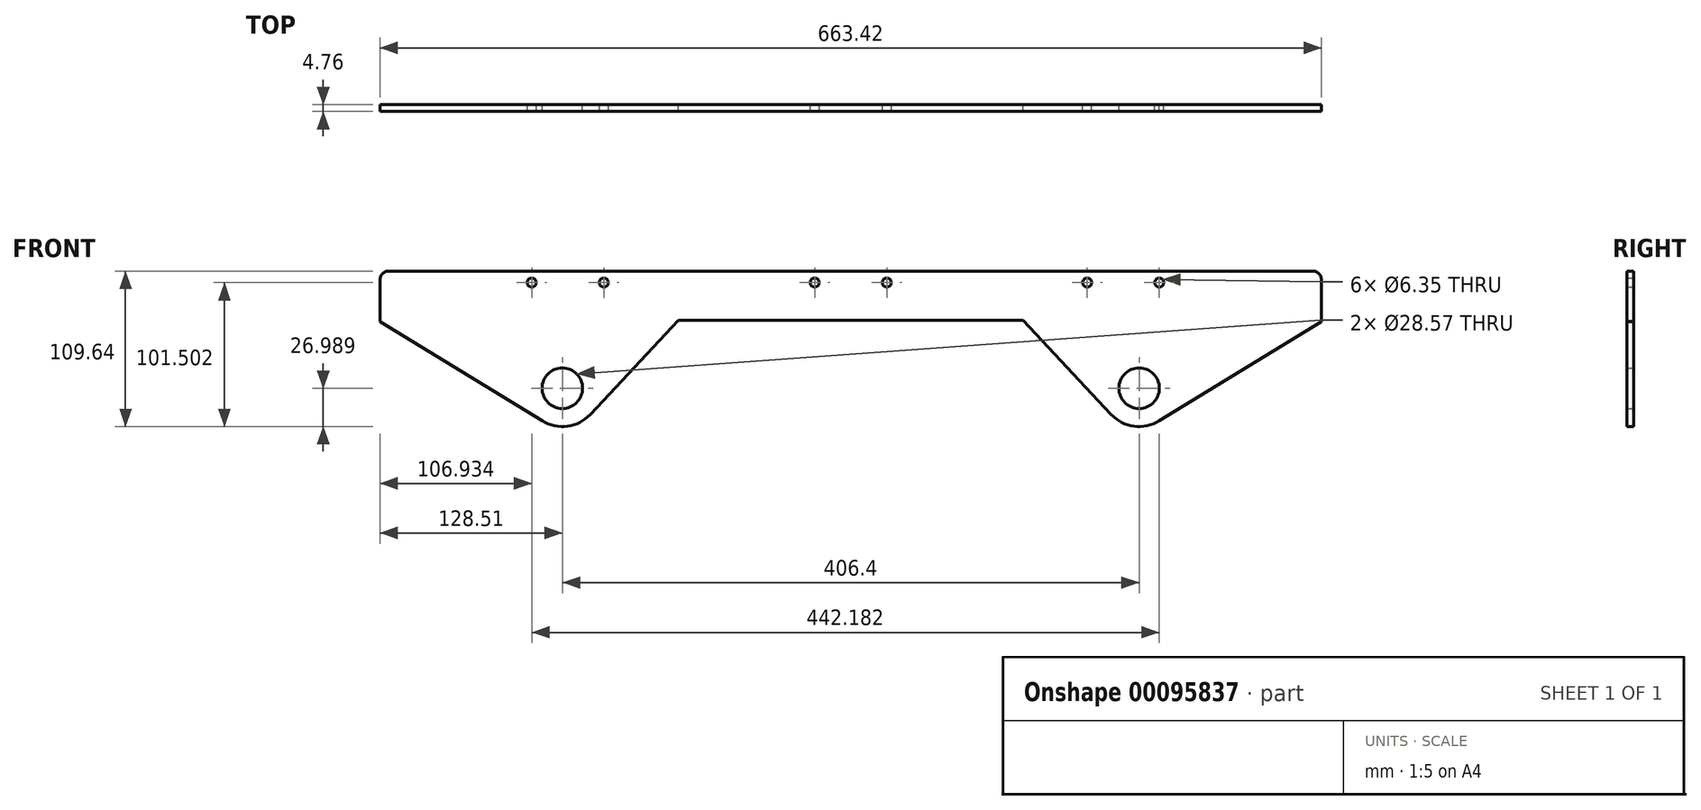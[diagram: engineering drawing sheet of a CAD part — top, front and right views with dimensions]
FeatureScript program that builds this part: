
annotation { "Feature Type Name" : "Feature", "Feature Type Description" : "" }
export const myFeature = defineFeature(function(context is Context, id is Id, definition is map)
    precondition{}
    {
        {
            var Q0;
            Q0=qCreatedBy(makeId("Front.planeOp"),FACE);
            var sketch = newSketch(context, id + "F0", { "sketchPlane" : qUnion([Q0])});
            skLineSegment(sketch, "E0", {"start": v(678.42, -37.96) * mm, "end": v(-454, -37.96) * mm, "construction": true});
            skLineSegment(sketch, "E1", {"start": v(0, -37.96) * mm, "end": v(0, 332.54) * mm, "construction": true});
            skCircle(sketch, "E2", {"center": v(217.4, 112.75) * mm, "radius": 3.18 * mm});
            skCircle(sketch, "E3", {"center": v(166.6, 112.75) * mm, "radius": 3.18 * mm});
            skCircle(sketch, "E4", {"center": v(25.4, 112.75) * mm, "radius": 3.18 * mm});
            skLineSegment(sketch, "E5", {"start": v(331.7, 85.33) * mm, "end": v(331.7, 114.54) * mm});
            skPoint(sketch, "E6.visualSharp", {"position": v(331.7, 119.1) * mm});
            skArc(sketch, "E6.filletArc", {"start": v(331.7, 114.54) * mm, "mid": v(329.85, 119.03) * mm, "end": v(325.36, 120.9) * mm});
            skPoint(sketch, "E7.orphan", {"position": v(0, -22.86) * mm});
            skLineSegment(sketch, "E8", {"start": v(325.36, 120.9) * mm, "end": v(0, 120.9) * mm});
            skLineSegment(sketch, "E9.MirrorCS", {"start": v(-325.36, 120.9) * mm, "end": v(0, 120.9) * mm});
            skArc(sketch, "E10.MirrorCS", {"start": v(-331.7, 114.54) * mm, "mid": v(-329.85, 119.03) * mm, "end": v(-325.36, 120.9) * mm});
            skLineSegment(sketch, "E11.MirrorCS", {"start": v(-331.7, 85.33) * mm, "end": v(-331.7, 114.54) * mm});
            skCircle(sketch, "E12.MirrorC", {"center": v(-25.4, 112.75) * mm, "radius": 3.18 * mm});
            skCircle(sketch, "E13.MirrorC", {"center": v(-173.98, 112.75) * mm, "radius": 3.18 * mm});
            skCircle(sketch, "E14.MirrorC", {"center": v(-224.78, 112.75) * mm, "radius": 3.18 * mm});
            skLineSegment(sketch, "E15", {"start": v(338.06, -37.96) * mm, "end": v(720.92, -140.55) * mm, "construction": true});
            skLineSegment(sketch, "E16", {"start": v(338.06, -37.96) * mm, "end": v(354.5, 23.38) * mm, "construction": true});
            skLineSegment(sketch, "E17", {"start": v(354.5, 23.38) * mm, "end": v(391.3, 13.51) * mm, "construction": true});
            skLineSegment(sketch, "E18", {"start": v(391.3, 13.51) * mm, "end": v(374.86, -47.82) * mm, "construction": true});
            skLineSegment(sketch, "E19", {"start": v(338.06, -37.96) * mm, "end": v(368.5, 75.63) * mm, "construction": true});
            skLineSegment(sketch, "E20", {"start": v(368.5, 75.63) * mm, "end": v(497.3, 41.12) * mm, "construction": true});
            skLineSegment(sketch, "E21", {"start": v(497.3, 41.12) * mm, "end": v(466.86, -72.47) * mm, "construction": true});
            skLineSegment(sketch, "E22", {"start": v(338.06, -37.96) * mm, "end": v(1103.17, -37.96) * mm});
            skCircle(sketch, "E23", {"center": v(203.2, 38.24) * mm, "radius": 14.29 * mm});
            skCircle(sketch, "E24", {"center": v(203.2, 38.24) * mm, "radius": 76.2 * mm, "construction": true});
            skArc(sketch, "E25.0", {"start": v(183.5, 19.79) * mm, "mid": v(199.6, 11.5) * mm, "end": v(217.3, 15.23) * mm});
            skLineSegment(sketch, "E26", {"start": v(331.7, 85.33) * mm, "end": v(217.3, 15.23) * mm});
            skLineSegment(sketch, "E27", {"start": v(0, 120.9) * mm, "end": v(0, 86.1) * mm, "construction": true});
            skLineSegment(sketch, "E28", {"start": v(0, 86.1) * mm, "end": v(121.38, 86.1) * mm});
            skLineSegment(sketch, "E29", {"start": v(121.38, 86.1) * mm, "end": v(183.5, 19.79) * mm});
            skLineSegment(sketch, "E30.MirrorCS", {"start": v(0, 86.1) * mm, "end": v(-121.38, 86.1) * mm});
            skLineSegment(sketch, "E31.MirrorCS", {"start": v(-121.38, 86.1) * mm, "end": v(-183.5, 19.79) * mm});
            skArc(sketch, "E32.MirrorCS", {"start": v(-183.5, 19.79) * mm, "mid": v(-199.6, 11.5) * mm, "end": v(-217.3, 15.23) * mm});
            skCircle(sketch, "E33.MirrorC", {"center": v(-203.2, 38.24) * mm, "radius": 14.29 * mm});
            skLineSegment(sketch, "E34.MirrorCS", {"start": v(-331.7, 85.33) * mm, "end": v(-217.3, 15.23) * mm});
            skCircle(sketch, "E35.MirrorC", {"center": v(-203.2, 38.24) * mm, "radius": 76.2 * mm, "construction": true});
            skSolve(sketch);
        }
        {
            var Q0;
            Q0=makeQuery(id+"F0.imprint","IMPRINT",FACE,{"disambiguationData":[TD([[makeQuery(id+"F0.imprint","IMPRINT",EDGE,{"derivedFrom":sQuery(id+"F0.wireOp",EDGE,"2147f539-64ec-4d1e-90c2-0bfce48f39d6")}),-1.0]])]});
            var Q1;
            Q1=makeQuery(id+"F0.imprint","IMPRINT",FACE,{"disambiguationData":[TD([[makeQuery(id+"F0.imprint","IMPRINT",EDGE,{"derivedFrom":sQuery(id+"F0.wireOp",EDGE,"E2")}),-1.0]])]});
            extrude(context, id + "F1", {"entities" : qUnion([Q0, Q1]), "depth" : 4.76 * mm});
        }
    });
